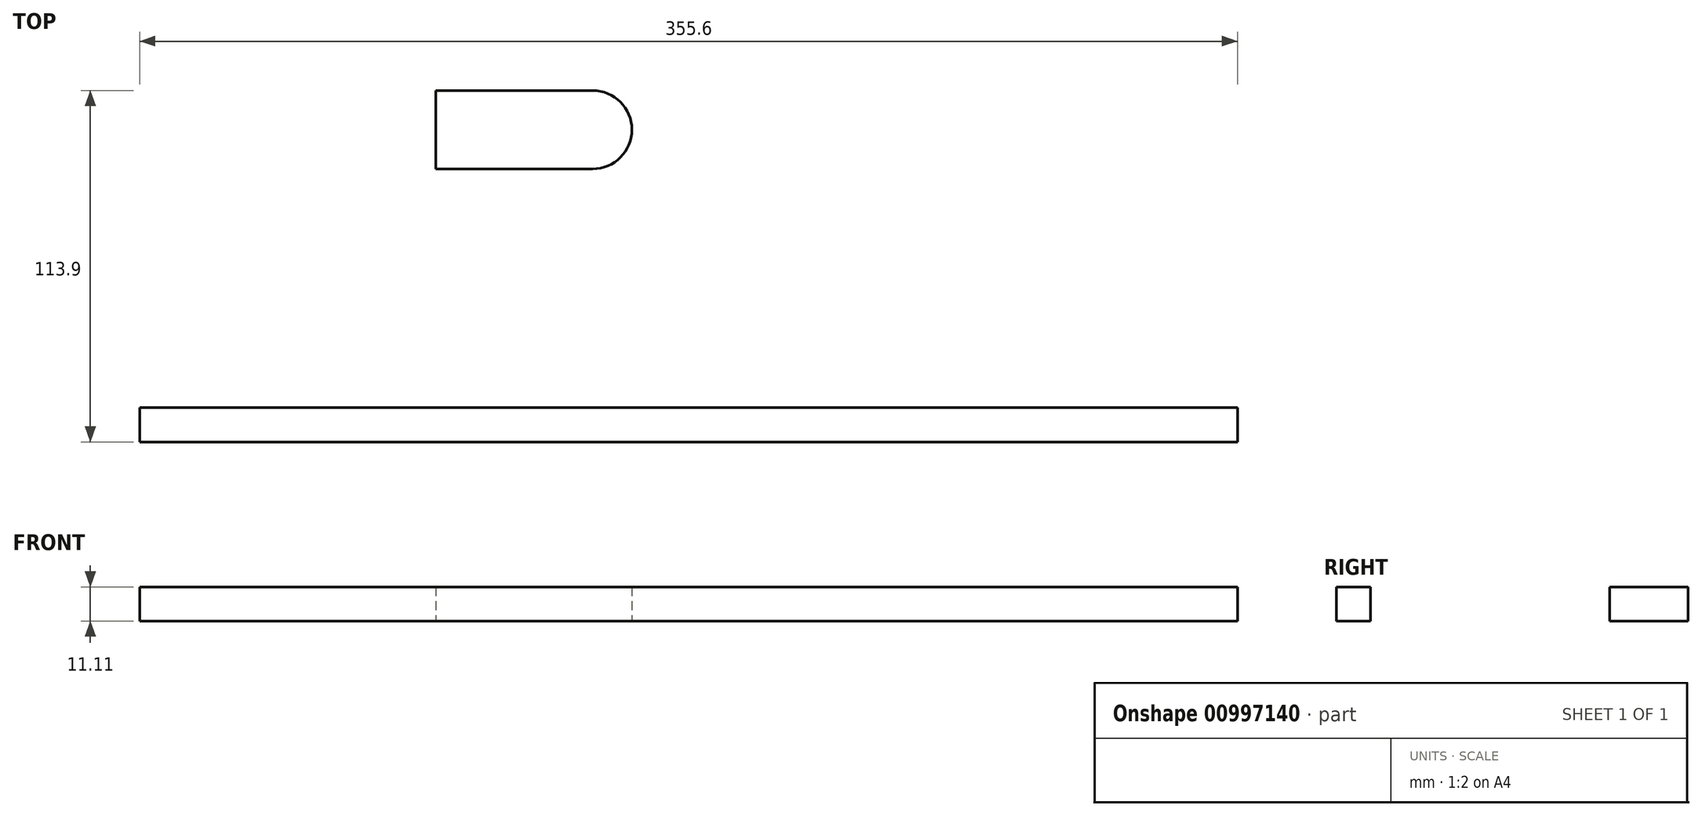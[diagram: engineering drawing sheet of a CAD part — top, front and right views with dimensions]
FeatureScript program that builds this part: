
annotation { "Feature Type Name" : "Feature", "Feature Type Description" : "" }
export const myFeature = defineFeature(function(context is Context, id is Id, definition is map)
    precondition{}
    {
        {
            var Q0;
            Q0=qCreatedBy(makeId("Top.planeOp"),FACE);
            var sketch = newSketch(context, id + "F0", { "sketchPlane" : qUnion([Q0])});
            skLineSegment(sketch, "E0", {"start": v(-80.83, -65.13) * mm, "end": v(274.77, -65.13) * mm});
            skLineSegment(sketch, "E1", {"start": v(274.77, -65.13) * mm, "end": v(274.77, -54.02) * mm});
            skLineSegment(sketch, "E2", {"start": v(-80.83, -65.13) * mm, "end": v(-80.83, -54.02) * mm});
            skLineSegment(sketch, "E3", {"start": v(-80.83, -54.02) * mm, "end": v(274.77, -54.02) * mm});
            skSolve(sketch);
        }
        {
            var Q0;
            Q0 = qSketchRegion(id + "F0", true);
            extrude(context, id + "F1", {"entities" : qUnion([Q0]), "depth" : 11.1 * mm, "offsetDistance" : 25.4 * mm});
        }
        {
            var Q0;
            Q0=qCreatedBy(makeId("Top.planeOp"),FACE);
            var sketch = newSketch(context, id + "F2", { "sketchPlane" : qUnion([Q0])});
            skLineSegment(sketch, "E4", {"start": v(15.08, 23.37) * mm, "end": v(65.88, 23.37) * mm});
            skLineSegment(sketch, "E5", {"start": v(65.88, 48.77) * mm, "end": v(15.08, 48.77) * mm});
            skLineSegment(sketch, "E6", {"start": v(15.08, 48.77) * mm, "end": v(15.08, 23.37) * mm});
            skArc(sketch, "E7", {"start": v(65.88, 48.77) * mm, "mid": v(78.58, 36.07) * mm, "end": v(65.88, 23.37) * mm});
            skSolve(sketch);
        }
        {
            var Q0;
            Q0 = qSketchRegion(id + "F2", true);
            extrude(context, id + "F3", {"entities" : qUnion([Q0]), "depth" : 11.1 * mm, "offsetDistance" : 25.4 * mm});
        }
        {
            var Q0;
            Q0=makeQuery(id+"F3.opExtrude","SWEPT_BODY",BODY,{"disambiguationData":[OSD([sQuery(id+"F2.wireOp",EDGE,"E4"),sQuery(id+"F2.wireOp",EDGE,"E5"),sQuery(id+"F2.wireOp",EDGE,"E6"),sQuery(id+"F2.wireOp",EDGE,"E7")])]});
            transform(context, id + "F4", {"entities" : qUnion([Q0]), "transformType" : TransformType.TRANSLATION_3D, "dx" : 0 * mm, "dy" : 0 * mm, "dz" : 0 * mm, "makeCopy" : true});
        }
    });
